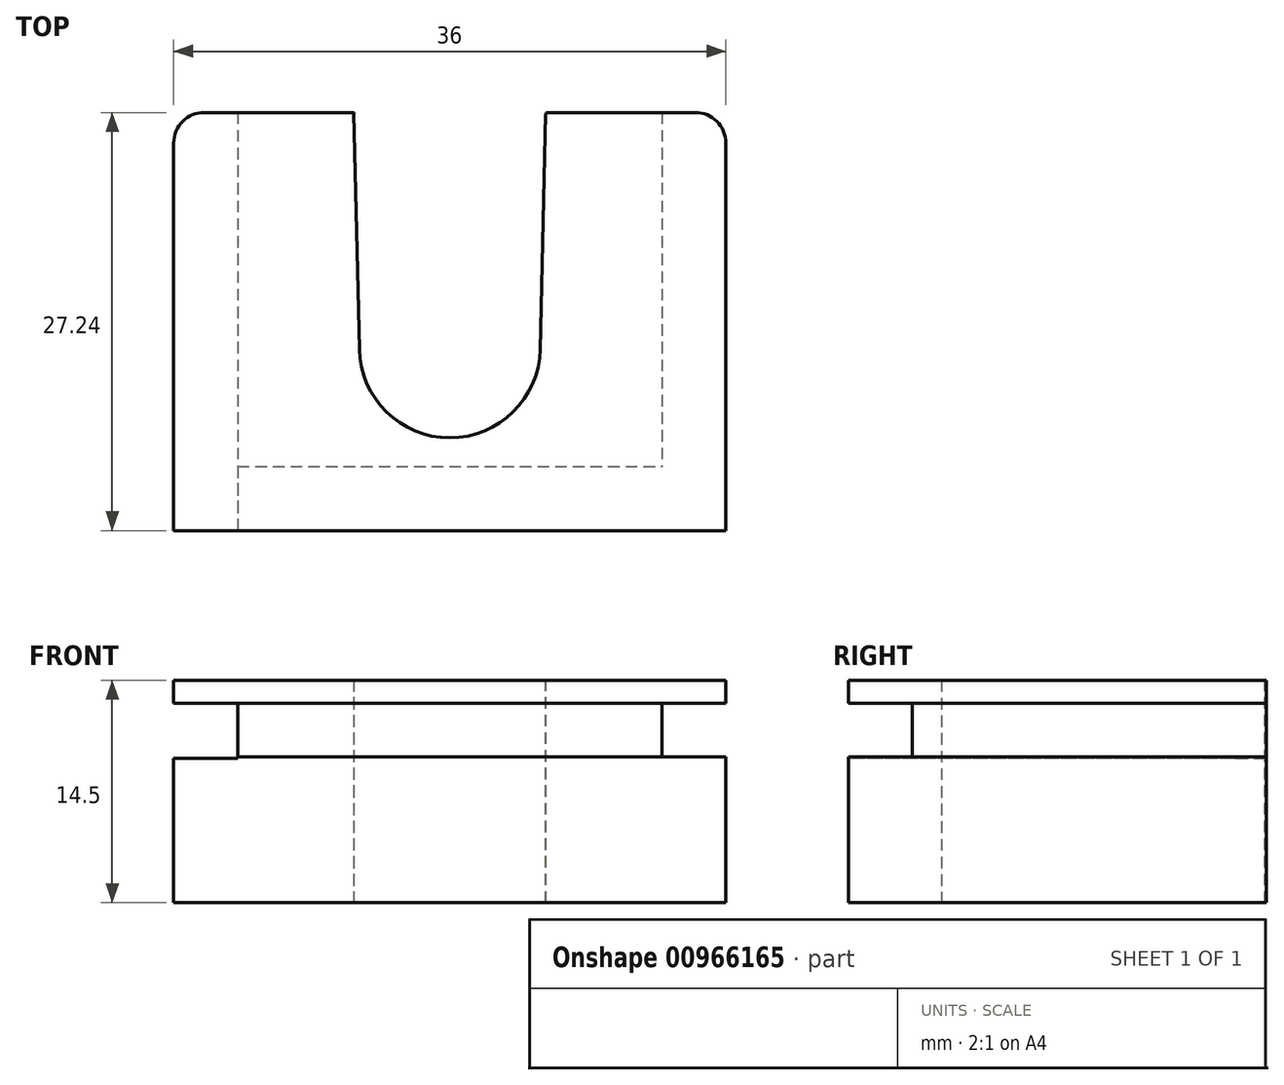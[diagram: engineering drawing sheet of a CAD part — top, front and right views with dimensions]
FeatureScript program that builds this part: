
annotation { "Feature Type Name" : "Feature", "Feature Type Description" : "" }
export const myFeature = defineFeature(function(context is Context, id is Id, definition is map)
    precondition{}
    {
        {
            var Q0;
            Q0=qCreatedBy(makeId("Top.planeOp"),FACE);
            var sketch = newSketch(context, id + "F0", { "sketchPlane" : qUnion([Q0])});
            skLineSegment(sketch, "E0.bottom", {"start": v(-18, -13.62) * mm, "end": v(18, -13.62) * mm});
            skLineSegment(sketch, "E0.top", {"start": v(-16, 13.62) * mm, "end": v(16, 13.62) * mm});
            skLineSegment(sketch, "E0.left", {"start": v(-18, -13.62) * mm, "end": v(-18, 11.62) * mm});
            skLineSegment(sketch, "E0.right", {"start": v(18, -13.62) * mm, "end": v(18, 11.62) * mm});
            skPoint(sketch, "E0.middle", {"position": v(0, 0) * mm});
            skCircle(sketch, "E1", {"center": v(0, -1.68) * mm, "radius": 5.9 * mm});
            skLineSegment(sketch, "E2", {"start": v(-6.25, 13.58) * mm, "end": v(6.25, 13.58) * mm});
            skLineSegment(sketch, "E3", {"start": v(-6.25, 13.58) * mm, "end": v(-5.9, -1.8) * mm});
            skLineSegment(sketch, "E4", {"start": v(6.25, 13.58) * mm, "end": v(5.9, -1.8) * mm});
            skPoint(sketch, "E5.visualSharp", {"position": v(-18, 13.62) * mm});
            skArc(sketch, "E5.filletArc", {"start": v(-16, 13.62) * mm, "mid": v(-17.41, 13.04) * mm, "end": v(-18, 11.62) * mm});
            skPoint(sketch, "E6.visualSharp", {"position": v(18, 13.62) * mm});
            skArc(sketch, "E6.filletArc", {"start": v(18, 11.62) * mm, "mid": v(17.41, 13.04) * mm, "end": v(16, 13.62) * mm});
            skSolve(sketch);
        }
        {
            var Q0;
            Q0 = qSketchRegion(id + "F0", true);
            extrude(context, id + "F1", {"entities" : qUnion([Q0]), "depth" : 14.5 * mm, "offsetDistance" : 25 * mm});
        }
        {
            var Q0;
            Q0=makeQuery(id+"F1.opExtrude","SWEPT_FACE",FACE,{"disambiguationData":[OSD([sQuery(id+"F0.wireOp",EDGE,"E0.top")])]});
            var sketch = newSketch(context, id + "F2", { "sketchPlane" : qUnion([Q0])});
            skLineSegment(sketch, "E7.bottom", {"start": v(6.23, 0) * mm, "end": v(-6.27, 0) * mm});
            skLineSegment(sketch, "E7.top", {"start": v(6.23, 14.5) * mm, "end": v(-6.27, 14.5) * mm});
            skLineSegment(sketch, "E7.left", {"start": v(6.23, 0) * mm, "end": v(6.23, 14.5) * mm});
            skLineSegment(sketch, "E7.right", {"start": v(-6.27, 0) * mm, "end": v(-6.27, 14.5) * mm});
            skSolve(sketch);
        }
        {
            var Q0;
            Q0=makeQuery(id+"F2.imprint","IMPRINT",FACE,{"disambiguationData":[TD([[makeQuery(id+"F2.imprint","IMPRINT",EDGE,{"derivedFrom":sQuery(id+"F2.wireOp",EDGE,"E7.bottom")}),-1.0]])]});
            extrude(context, id + "F3", {"entities" : qUnion([Q0]), "operationType" : NewBodyOperationType.REMOVE, "oppositeDirection" : true, "depth" : 0.1 * mm, "offsetDistance" : 25 * mm});
        }
        {
            var Q0;
            Q0=makeQuery(id+"F1.opExtrude","SWEPT_FACE",FACE,{"disambiguationData":[OSD([sQuery(id+"F0.wireOp",EDGE,"E0.right")])]});
            var sketch = newSketch(context, id + "F4", { "sketchPlane" : qUnion([Q0])});
            skLineSegment(sketch, "E8.bottom", {"start": v(13.62, 9.5) * mm, "end": v(-13.63, 9.5) * mm});
            skLineSegment(sketch, "E8.top", {"start": v(13.62, 13) * mm, "end": v(-13.63, 13) * mm});
            skLineSegment(sketch, "E8.left", {"start": v(13.62, 9.5) * mm, "end": v(13.62, 13) * mm});
            skLineSegment(sketch, "E8.right", {"start": v(-13.63, 9.5) * mm, "end": v(-13.63, 13) * mm});
            skSolve(sketch);
        }
        {
            var Q0;
            Q0=makeQuery(id+"F4.imprint","IMPRINT",FACE,{"disambiguationData":[TD([[makeQuery(id+"F4.imprint","IMPRINT",EDGE,{"derivedFrom":sQuery(id+"F4.wireOp",EDGE,"E8.bottom")}),-1.0]])]});
            extrude(context, id + "F5", {"entities" : qUnion([Q0]), "operationType" : NewBodyOperationType.REMOVE, "oppositeDirection" : true, "depth" : 4.17 * mm, "offsetDistance" : 25 * mm});
        }
        {
            var Q0;
            Q0=makeQuery(id+"F1.opExtrude","SWEPT_FACE",FACE,{"disambiguationData":[OSD([sQuery(id+"F0.wireOp",EDGE,"E0.left")])]});
            var sketch = newSketch(context, id + "F6", { "sketchPlane" : qUnion([Q0])});
            skLineSegment(sketch, "E9.bottom", {"start": v(-13.63, 9.4) * mm, "end": v(13.62, 9.4) * mm});
            skLineSegment(sketch, "E9.top", {"start": v(-13.63, 13) * mm, "end": v(13.62, 13) * mm});
            skLineSegment(sketch, "E9.left", {"start": v(-13.63, 9.4) * mm, "end": v(-13.63, 13) * mm});
            skLineSegment(sketch, "E9.right", {"start": v(13.62, 9.4) * mm, "end": v(13.62, 13) * mm});
            skSolve(sketch);
        }
        {
            var Q0;
            Q0=makeQuery(id+"F6.imprint","IMPRINT",FACE,{"disambiguationData":[TD([[makeQuery(id+"F6.imprint","IMPRINT",EDGE,{"derivedFrom":sQuery(id+"F6.wireOp",EDGE,"E9.bottom")}),1.0]])]});
            extrude(context, id + "F7", {"entities" : qUnion([Q0]), "operationType" : NewBodyOperationType.REMOVE, "oppositeDirection" : true, "depth" : 4.17 * mm, "offsetDistance" : 25 * mm});
        }
        {
            var Q0;
            Q0=makeQuery(id+"F1.opExtrude","SWEPT_FACE",FACE,{"disambiguationData":[OSD([sQuery(id+"F0.wireOp",EDGE,"E0.bottom")])]});
            var sketch = newSketch(context, id + "F8", { "sketchPlane" : qUnion([Q0])});
            skLineSegment(sketch, "E10.bottom", {"start": v(-13.83, 13) * mm, "end": v(13.83, 13) * mm});
            skLineSegment(sketch, "E10.top", {"start": v(-13.83, 9.5) * mm, "end": v(13.83, 9.5) * mm});
            skLineSegment(sketch, "E10.left", {"start": v(-13.83, 13) * mm, "end": v(-13.83, 9.5) * mm});
            skLineSegment(sketch, "E10.right", {"start": v(13.83, 13) * mm, "end": v(13.83, 9.5) * mm});
            skSolve(sketch);
        }
        {
            var Q0;
            Q0=makeQuery(id+"F8.imprint","IMPRINT",FACE,{"disambiguationData":[TD([[makeQuery(id+"F8.imprint","IMPRINT",EDGE,{"derivedFrom":sQuery(id+"F8.wireOp",EDGE,"E10.bottom")}),-1.0]])]});
            extrude(context, id + "F9", {"entities" : qUnion([Q0]), "operationType" : NewBodyOperationType.REMOVE, "oppositeDirection" : true, "depth" : 4.17 * mm, "offsetDistance" : 25 * mm});
        }
    });
